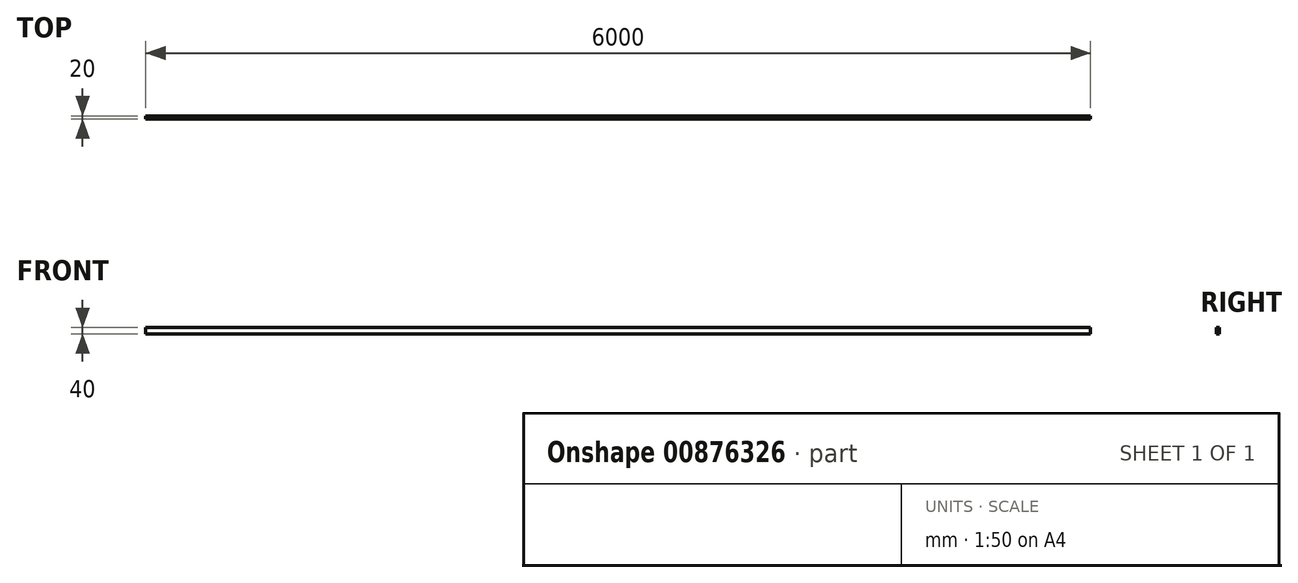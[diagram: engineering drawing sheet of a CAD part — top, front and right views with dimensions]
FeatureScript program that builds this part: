
annotation { "Feature Type Name" : "Feature", "Feature Type Description" : "" }
export const myFeature = defineFeature(function(context is Context, id is Id, definition is map)
    precondition{}
    {
        {
            var Q0;
            Q0=qCreatedBy(makeId("Right.planeOp"),FACE);
            var sketch = newSketch(context, id + "F0", { "sketchPlane" : qUnion([Q0])});
            skLineSegment(sketch, "E0", {"start": v(0, 0) * mm, "end": v(0, 40) * mm});
            skLineSegment(sketch, "E1", {"start": v(0, 40) * mm, "end": v(-20, 40) * mm});
            skLineSegment(sketch, "E2", {"start": v(-20, 40) * mm, "end": v(-20, 0) * mm});
            skLineSegment(sketch, "E3", {"start": v(-20, 0) * mm, "end": v(0, 0) * mm});
            skSolve(sketch);
        }
        {
            var Q0;
            Q0=qCreatedBy(makeId("Front.planeOp"),FACE);
            var sketch = newSketch(context, id + "F1", { "sketchPlane" : qUnion([Q0])});
            skLineSegment(sketch, "E4", {"start": v(0, 0) * mm, "end": v(-6000, 0) * mm});
            skSolve(sketch);
        }
        {
            var Q0;
            Q0=makeQuery(id+"F0.imprint","IMPRINT",FACE,{"disambiguationData":[TD([[makeQuery(id+"F0.imprint","IMPRINT",EDGE,{"derivedFrom":sQuery(id+"F0.wireOp",EDGE,"E0")}),1.0]])]});
            var Q1;
            Q1=sQuery(id+"F1.wireOp",EDGE,"E4");
            sweep(context, id + "F2", {"profiles" : qUnion([Q0]), "path" : qUnion([Q1])});
        }
    });
